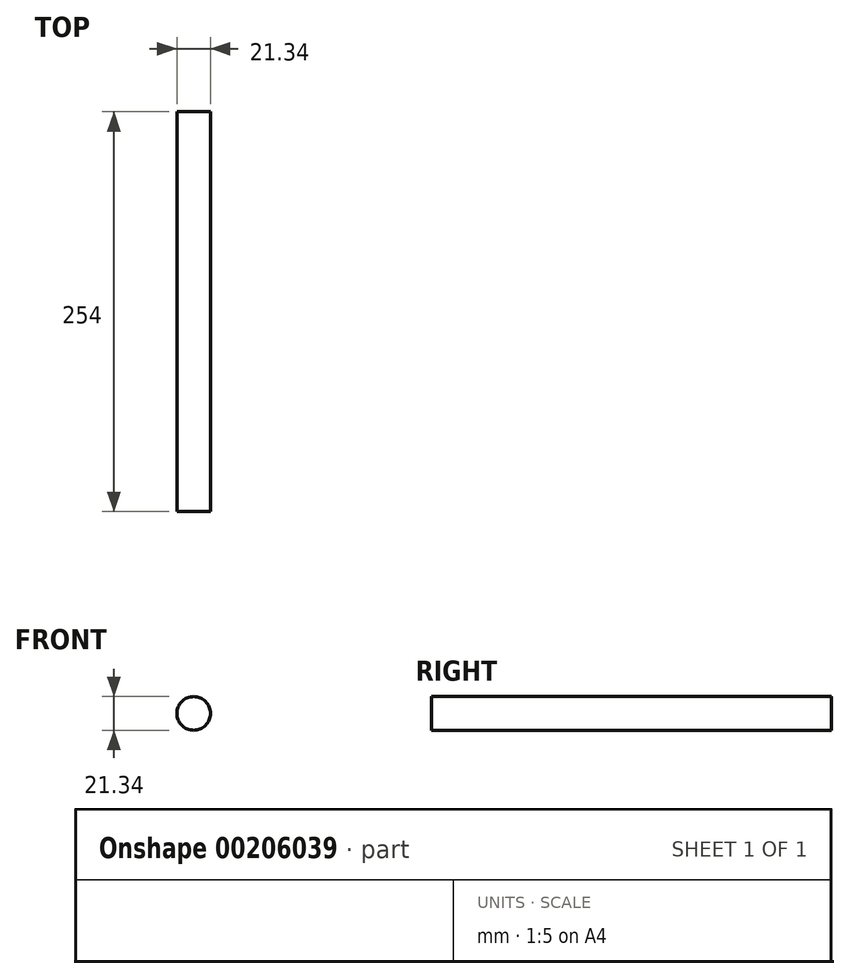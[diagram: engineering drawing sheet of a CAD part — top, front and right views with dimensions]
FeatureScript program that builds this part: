
annotation { "Feature Type Name" : "Feature", "Feature Type Description" : "" }
export const myFeature = defineFeature(function(context is Context, id is Id, definition is map)
    precondition{}
    {
        {
            var Q0;
            Q0=qCreatedBy(makeId("Front.planeOp"),FACE);
            var sketch = newSketch(context, id + "F0", { "sketchPlane" : qUnion([Q0])});
            skCircle(sketch, "E0", {"center": v(0, 0) * mm, "radius": 10.67 * mm});
            skSolve(sketch);
        }
        {
            var Q0;
            Q0=makeQuery(id+"F0.imprint","IMPRINT",FACE,{"disambiguationData":[TD([[makeQuery(id+"F0.imprint","IMPRINT",EDGE,{"derivedFrom":sQuery(id+"F0.wireOp",EDGE,"E0")}),1.0]])]});
            extrude(context, id + "F1", {"entities" : qUnion([Q0]), "depth" : 254 * mm});
        }
    });
